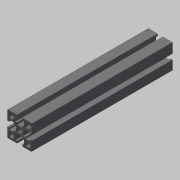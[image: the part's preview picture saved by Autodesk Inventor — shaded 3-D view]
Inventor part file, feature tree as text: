
AUTODESK INVENTOR PART (.ipt)
format: ipt  version: 2021.2 (Build 252289000, 289)  size: 203,776 bytes
history: native  units: in
note: dims shown in document units (in); Inventor stores cm internally (conversion verified against a paired STEP export)
features: other x2, extrude x1, sketch x1, projected_geometry x1
ambient origin geometry x8: Origin, YZ Plane, XZ Plane, XY Plane, X Axis, Y Axis, Z Axis, Center Point
bodies: Body1 (feature_tree)
feature tree (5):
  other  "ソリッド2"
  extrude  "押し出し1"  Depth=6.6929in
  sketch  "スケッチ2"
  projected_geometry  "投影ループ1"
  other  "ソリッド1"
